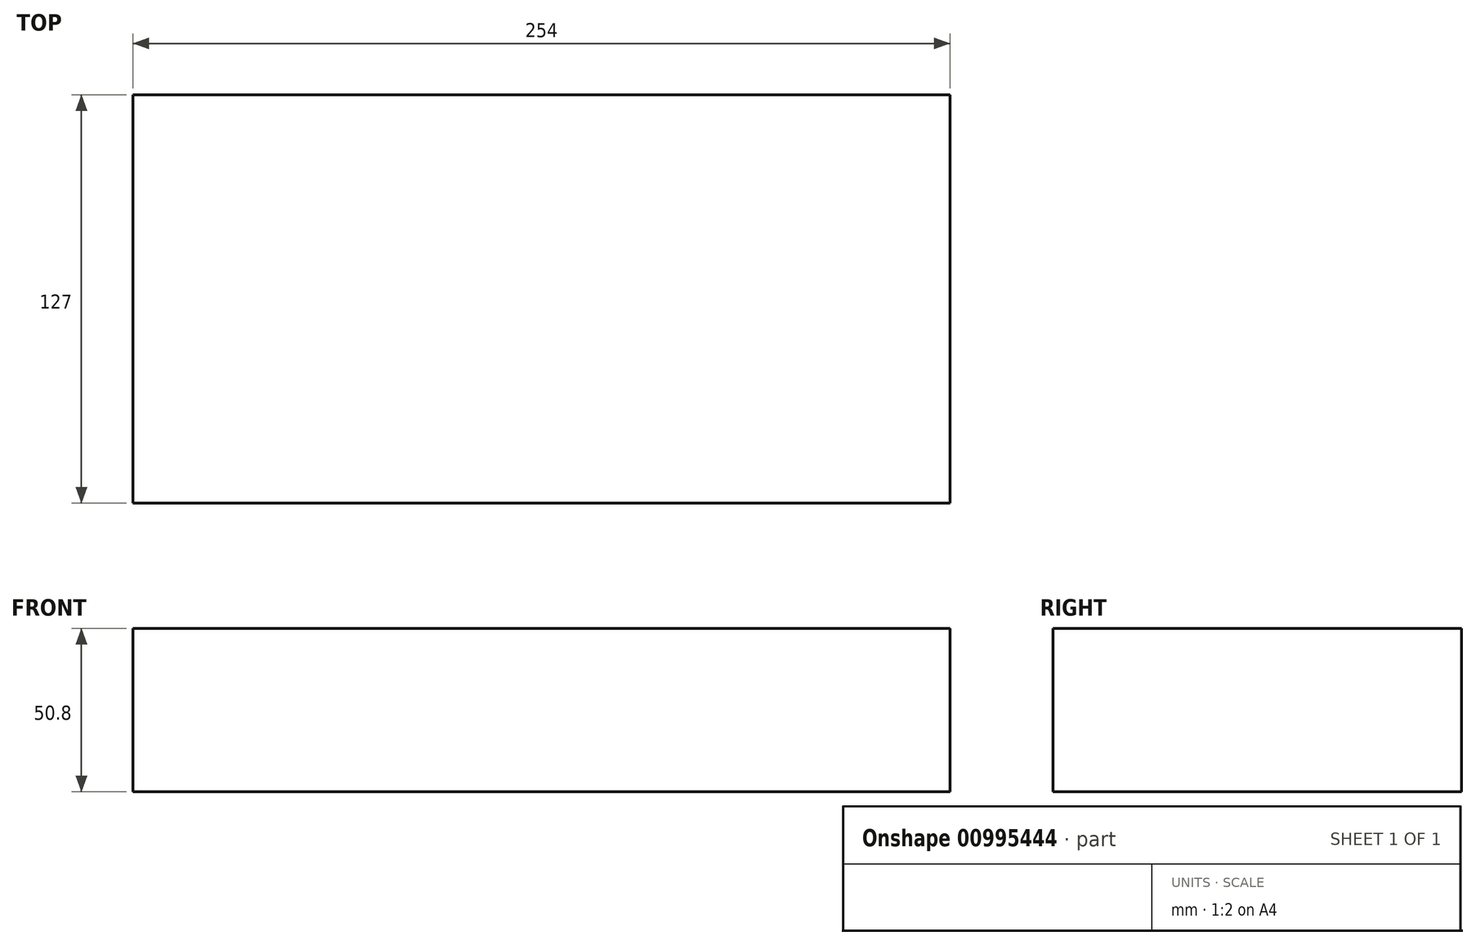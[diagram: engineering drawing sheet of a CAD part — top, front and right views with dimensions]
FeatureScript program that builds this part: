
annotation { "Feature Type Name" : "Feature", "Feature Type Description" : "" }
export const myFeature = defineFeature(function(context is Context, id is Id, definition is map)
    precondition{}
    {
        {
            var Q0;
            Q0=qCreatedBy(makeId("Top.planeOp"),FACE);
            var sketch = newSketch(context, id + "F0", { "sketchPlane" : qUnion([Q0])});
            skLineSegment(sketch, "E0.bottom", {"start": v(127, -63.5) * mm, "end": v(-127, -63.5) * mm});
            skLineSegment(sketch, "E0.top", {"start": v(127, 63.5) * mm, "end": v(-127, 63.5) * mm});
            skLineSegment(sketch, "E0.left", {"start": v(127, -63.5) * mm, "end": v(127, 63.5) * mm});
            skLineSegment(sketch, "E0.right", {"start": v(-127, -63.5) * mm, "end": v(-127, 63.5) * mm});
            skPoint(sketch, "E0.middle", {"position": v(0, 0) * mm});
            skSolve(sketch);
        }
        {
            var Q0;
            Q0 = qSketchRegion(id + "F0", true);
            extrude(context, id + "F1", {"entities" : qUnion([Q0]), "depth" : 50.8 * mm, "offsetDistance" : 25.4 * mm});
        }
    });
